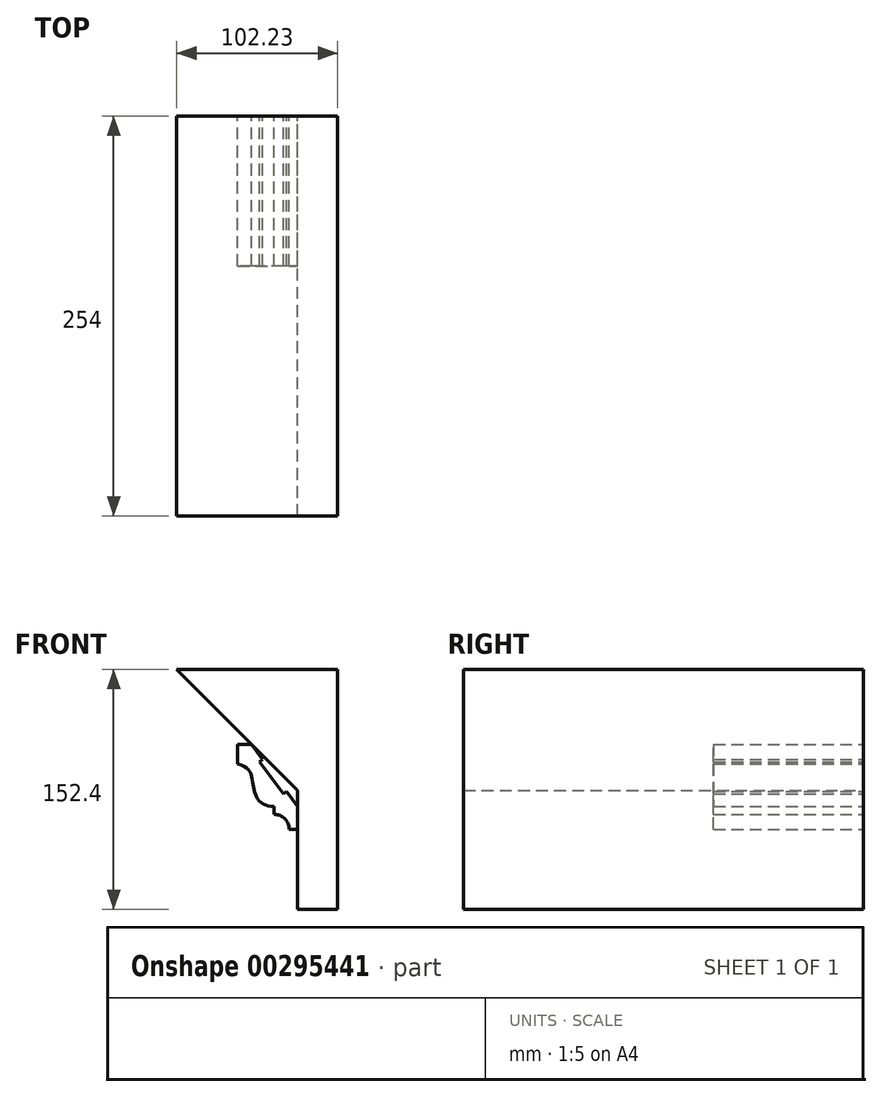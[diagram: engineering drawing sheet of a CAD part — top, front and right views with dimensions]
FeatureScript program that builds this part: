
annotation { "Feature Type Name" : "Feature", "Feature Type Description" : "" }
export const myFeature = defineFeature(function(context is Context, id is Id, definition is map)
    precondition{}
    {
        {
            var Q0;
            Q0=qCreatedBy(makeId("Front.planeOp"),FACE);
            var sketch = newSketch(context, id + "F0", { "sketchPlane" : qUnion([Q0])});
            skLineSegment(sketch, "E0", {"start": v(-5.33, 0) * mm, "end": v(0, 0) * mm});
            skLineSegment(sketch, "E1", {"start": v(0, 0) * mm, "end": v(0, 14.48) * mm});
            skLineSegment(sketch, "E2", {"start": v(-29.2, 53.98) * mm, "end": v(-38.1, 53.98) * mm});
            skLineSegment(sketch, "E3", {"start": v(-38.1, 53.98) * mm, "end": v(-38.1, 41.66) * mm});
            skLineSegment(sketch, "E4", {"start": v(0, 14.48) * mm, "end": v(-7.05, 24.02) * mm});
            skLineSegment(sketch, "E5", {"start": v(-7.05, 24.02) * mm, "end": v(-9.1, 22.5) * mm});
            skLineSegment(sketch, "E6", {"start": v(-9.1, 22.5) * mm, "end": v(-24.2, 42.93) * mm});
            skLineSegment(sketch, "E7", {"start": v(-24.2, 42.93) * mm, "end": v(-22.16, 44.44) * mm});
            skLineSegment(sketch, "E8", {"start": v(-22.16, 44.44) * mm, "end": v(-29.2, 53.98) * mm});
            skLineSegment(sketch, "E9", {"start": v(-14.86, 9.53) * mm, "end": v(-14.86, 14.6) * mm});
            skArc(sketch, "E10", {"start": v(-5.33, 0) * mm, "mid": v(-8.12, 6.74) * mm, "end": v(-14.86, 9.53) * mm});
            skFitSpline(sketch, "E11", {"points": [v(-38.1, 41.66) * mm, v(-27.86, 25.6) * mm, v(-14.86, 14.6) * mm], "startDerivative": vector(58.03, -11.78) * mm, "endDerivative": vector(50.48, 1.67) * mm});
            skPoint(sketch, "E12.orphan", {"position": v(-38.1, 0) * mm});
            skSolve(sketch);
        }
        {
            var Q0;
            Q0 = qSketchRegion(id + "F0", true);
            extrude(context, id + "F1", {"entities" : qUnion([Q0]), "depth" : 95.25 * mm});
        }
        {
            var Q0;
            Q0=qCreatedBy(makeId("Front.planeOp"),FACE);
            var sketch = newSketch(context, id + "F2", { "sketchPlane" : qUnion([Q0])});
            skLineSegment(sketch, "E13", {"start": v(0, -50.8) * mm, "end": v(0, 24.77) * mm});
            skLineSegment(sketch, "E14", {"start": v(0, 24.77) * mm, "end": v(-76.83, 101.6) * mm});
            skLineSegment(sketch, "E15", {"start": v(-76.83, 101.6) * mm, "end": v(25.4, 101.6) * mm});
            skLineSegment(sketch, "E16", {"start": v(25.4, 101.6) * mm, "end": v(25.4, -50.8) * mm});
            skLineSegment(sketch, "E17", {"start": v(25.4, -50.8) * mm, "end": v(0, -50.8) * mm});
            skSolve(sketch);
        }
        {
            var Q0;
            Q0 = qSketchRegion(id + "F2", true);
            extrude(context, id + "F3", {"entities" : qUnion([Q0]), "depth" : 254 * mm});
        }
        {
            var Q0;
            Q0=qCreatedBy(makeId("Front.planeOp"),FACE);
            var sketch = newSketch(context, id + "F4", { "sketchPlane" : qUnion([Q0])});
            skLineSegment(sketch, "E18", {"start": v(0, 0) * mm, "end": v(0, -50.8) * mm});
            skLineSegment(sketch, "E19", {"start": v(0, -50.8) * mm, "end": v(-76.2, -50.8) * mm});
            skLineSegment(sketch, "E20", {"start": v(-76.2, -50.8) * mm, "end": v(-76.2, 101.6) * mm});
            skLineSegment(sketch, "E21", {"start": v(-76.83, 101.6) * mm, "end": v(-76.2, 101.6) * mm});
            skLineSegment(sketch, "E22", {"start": v(-76.83, 101.6) * mm, "end": v(-38.1, 62.87) * mm});
            skLineSegment(sketch, "E23", {"start": v(-38.1, 62.87) * mm, "end": v(-38.1, 30.48) * mm});
            skLineSegment(sketch, "E24", {"start": v(-7.62, 0) * mm, "end": v(0, 0) * mm});
            skLineSegment(sketch, "E25", {"start": v(-38.1, 30.48) * mm, "end": v(-7.62, 0) * mm});
            skPoint(sketch, "E26.orphan", {"position": v(-15.24, 0) * mm});
            skSolve(sketch);
        }
        {
            var Q0;
            Q0=makeQuery(id+"F1.opExtrude","SWEPT_BODY",BODY,{"disambiguationData":[OSD([sQuery(id+"F0.wireOp",EDGE,"E0"),sQuery(id+"F0.wireOp",EDGE,"E1"),sQuery(id+"F0.wireOp",EDGE,"E2"),sQuery(id+"F0.wireOp",EDGE,"E3"),sQuery(id+"F0.wireOp",EDGE,"E4"),sQuery(id+"F0.wireOp",EDGE,"E5"),sQuery(id+"F0.wireOp",EDGE,"E6"),sQuery(id+"F0.wireOp",EDGE,"E7"),sQuery(id+"F0.wireOp",EDGE,"E8"),sQuery(id+"F0.wireOp",EDGE,"E9"),sQuery(id+"F0.wireOp",EDGE,"E10"),sQuery(id+"F0.wireOp",EDGE,"E11")])]});
            transform(context, id + "F5", {"entities" : qUnion([Q0]), "transformType" : TransformType.TRANSLATION_3D, "dx" : 0 * mm, "dy" : 0 * mm, "dz" : 0 * mm, "makeCopy" : true});
        }
        {
            var Q0;
            Q0=makeQuery(id+"F1.opExtrude","SWEPT_BODY",BODY,{"disambiguationData":[OSD([sQuery(id+"F0.wireOp",EDGE,"E0"),sQuery(id+"F0.wireOp",EDGE,"E1"),sQuery(id+"F0.wireOp",EDGE,"E2"),sQuery(id+"F0.wireOp",EDGE,"E3"),sQuery(id+"F0.wireOp",EDGE,"E4"),sQuery(id+"F0.wireOp",EDGE,"E5"),sQuery(id+"F0.wireOp",EDGE,"E6"),sQuery(id+"F0.wireOp",EDGE,"E7"),sQuery(id+"F0.wireOp",EDGE,"E8"),sQuery(id+"F0.wireOp",EDGE,"E9"),sQuery(id+"F0.wireOp",EDGE,"E10"),sQuery(id+"F0.wireOp",EDGE,"E11")])]});
            transform(context, id + "F6", {"entities" : qUnion([Q0]), "transformType" : TransformType.TRANSLATION_3D, "dx" : 0 * mm, "dy" : 0 * mm, "dz" : 0 * mm, "makeCopy" : true});
        }
        {
            var Q0;
            Q0=makeQuery(id+"F6.opPattern","COPY",BODY,{"derivedFrom":makeQuery(id+"F1.opExtrude","SWEPT_BODY",BODY,{"disambiguationData":[OSD([sQuery(id+"F0.wireOp",EDGE,"E0"),sQuery(id+"F0.wireOp",EDGE,"E1"),sQuery(id+"F0.wireOp",EDGE,"E2"),sQuery(id+"F0.wireOp",EDGE,"E3"),sQuery(id+"F0.wireOp",EDGE,"E4"),sQuery(id+"F0.wireOp",EDGE,"E5"),sQuery(id+"F0.wireOp",EDGE,"E6"),sQuery(id+"F0.wireOp",EDGE,"E7"),sQuery(id+"F0.wireOp",EDGE,"E8"),sQuery(id+"F0.wireOp",EDGE,"E9"),sQuery(id+"F0.wireOp",EDGE,"E10"),sQuery(id+"F0.wireOp",EDGE,"E11")])]}),"instanceName":"1"});
            deleteBodies(context, id + "F7", {"entities" : qUnion([Q0])});
        }
        {
            var Q0;
            Q0=makeQuery(id+"F5.opPattern","COPY",BODY,{"derivedFrom":makeQuery(id+"F1.opExtrude","SWEPT_BODY",BODY,{"disambiguationData":[OSD([sQuery(id+"F0.wireOp",EDGE,"E0"),sQuery(id+"F0.wireOp",EDGE,"E1"),sQuery(id+"F0.wireOp",EDGE,"E2"),sQuery(id+"F0.wireOp",EDGE,"E3"),sQuery(id+"F0.wireOp",EDGE,"E4"),sQuery(id+"F0.wireOp",EDGE,"E5"),sQuery(id+"F0.wireOp",EDGE,"E6"),sQuery(id+"F0.wireOp",EDGE,"E7"),sQuery(id+"F0.wireOp",EDGE,"E8"),sQuery(id+"F0.wireOp",EDGE,"E9"),sQuery(id+"F0.wireOp",EDGE,"E10"),sQuery(id+"F0.wireOp",EDGE,"E11")])]}),"instanceName":"1"});
            deleteBodies(context, id + "F8", {"entities" : qUnion([Q0])});
        }
    });
